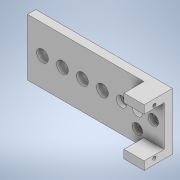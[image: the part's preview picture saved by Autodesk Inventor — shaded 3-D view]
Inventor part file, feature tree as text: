
AUTODESK INVENTOR PART (.ipt)
format: ipt  version: 2020 (Build 240168000, 168)  size: 400,384 bytes
history: native  units: in
note: dims shown in document units (in); Inventor stores cm internally (conversion verified against a paired STEP export)
features: extrude x9, sketch x9
ambient origin geometry x8: Origin, YZ Plane, XZ Plane, XY Plane, X Axis, Y Axis, Z Axis, Center Point
bodies: Solid1 (feature_tree)
feature tree (18):
  extrude  "Extrusion1"  Depth=1.2598in
  extrude  "Extrusion2"  Depth=0.1181in
  extrude  "Extrusion3"  Depth=1.5748in TaperAngle=360.0deg
  extrude  "Extrusion4"  Depth=0.1969in
  extrude  "Extrusion5"  Depth=0.0984in TaperAngle=0.0deg
  extrude  "Extrusion6"  Depth=0.1969in
  extrude  "Extrusion7"  Depth=0.4724in TaperAngle=0.0deg
  extrude  "Extrusion8"  Depth=0.3937in TaperAngle=0.0deg
  extrude  "Extrusion9"  Depth=0.4764in
  sketch  "Sketch1"  dims[d1=1.2598in d2=1.2598in]
  sketch  "Sketch2"  dims[d3=0.1969in d4=0.0in d5=0.1181in]
  sketch  "Sketch3"  dims[d6=0.374in d7=1.5748in d9=360.0deg]
  sketch  "Sketch4"  dims[d11=0.1969in d12=0.0in d13=0.2441in]
  sketch  "Sketch5"  dims[d14=1.5748in d16=360.0deg d18=0.0984in d19=0.0in]
  sketch  "Sketch8"  dims[d20=0.4764in d21=0.1969in]
  sketch  "Sketch9"  dims[d22=0.1969in d23=0.4724in d24=0.0in]
  sketch  "Sketch10"  dims[d25=0.2362in d26=0.3937in d27=0.0in]
  sketch  "Sketch11"  dims[d28=0.4764in d29=0.4764in d30=1.2598in d31=0.0433in d32=1.2598in d33=0.0433in d34=0.1969in d35=0.0in d36=0.2323in d37=0.5394in d38=0.0787in d39=0.5906in d40=0.0in d41=1.9685in d42=0.0in d43=0.1339in d44=0.1969in d45=0.4724in d46=0.4724in d47=0.4724in d48=0.2756in d49=0.2756in d50=0.2756in d51=0.2756in d52=1.9685in d53=0.0in]
